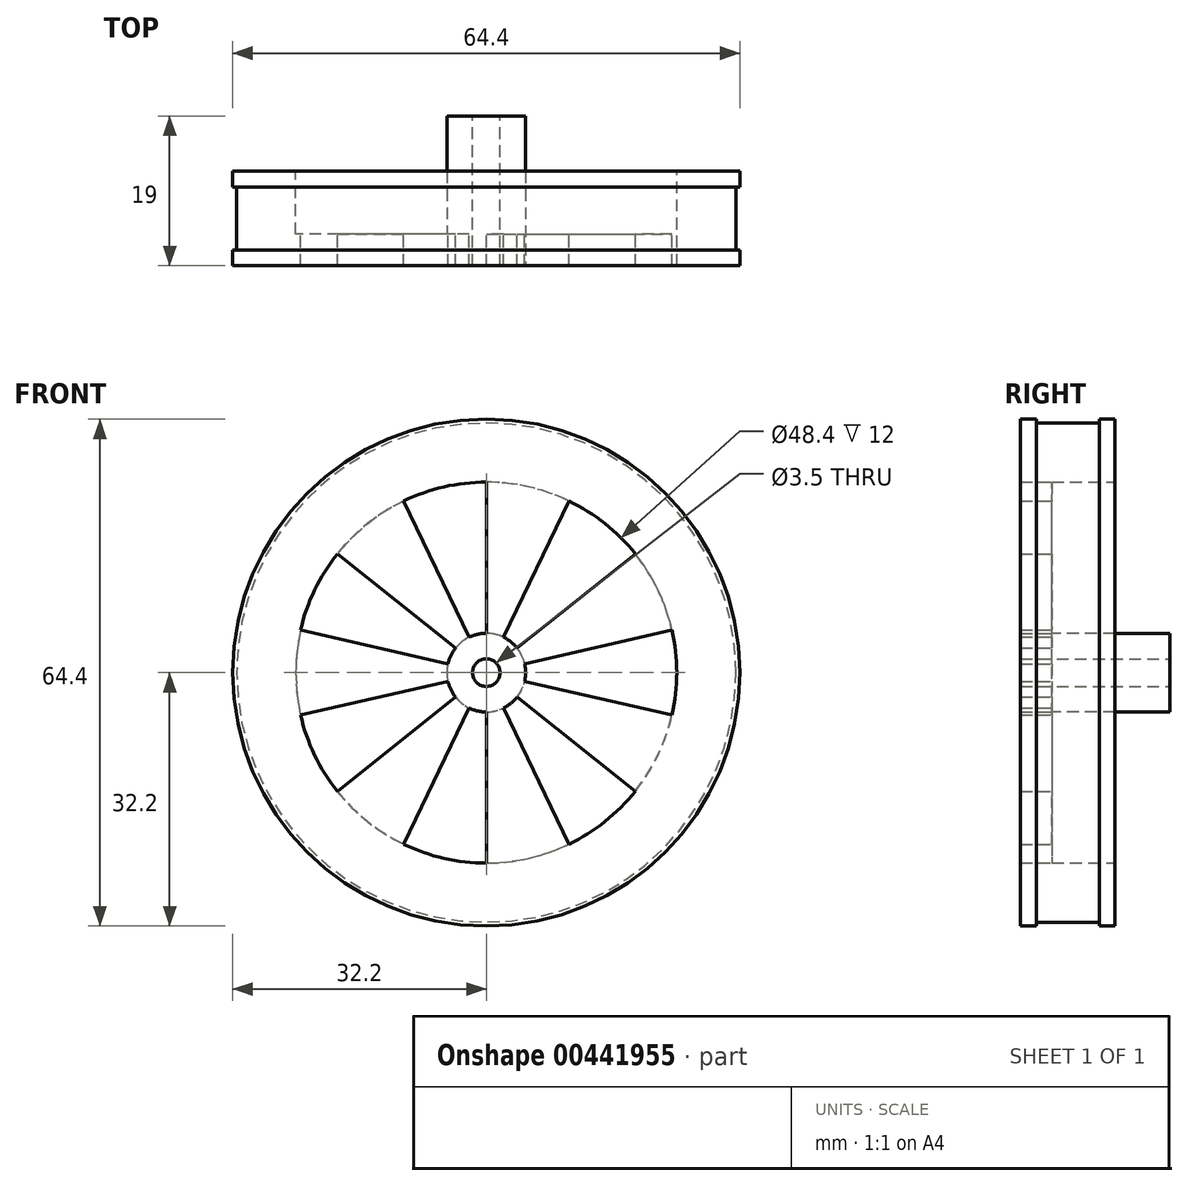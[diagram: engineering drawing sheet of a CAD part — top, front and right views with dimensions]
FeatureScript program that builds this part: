
annotation { "Feature Type Name" : "Feature", "Feature Type Description" : "" }
export const myFeature = defineFeature(function(context is Context, id is Id, definition is map)
    precondition{}
    {
        {
            var Q0;
            Q0=qCreatedBy(makeId("Top.planeOp"),FACE);
            var sketch = newSketch(context, id + "F0", { "sketchPlane" : qUnion([Q0])});
            skLineSegment(sketch, "E0", {"start": v(0, 0) * mm, "end": v(32.2, 0) * mm});
            skLineSegment(sketch, "E1", {"start": v(32.2, 0) * mm, "end": v(32.2, 2) * mm});
            skLineSegment(sketch, "E2", {"start": v(32.2, 2) * mm, "end": v(31.7, 2) * mm});
            skLineSegment(sketch, "E3", {"start": v(31.7, 2) * mm, "end": v(31.7, 10) * mm});
            skLineSegment(sketch, "E4", {"start": v(31.7, 10) * mm, "end": v(32.2, 10) * mm});
            skLineSegment(sketch, "E5", {"start": v(32.2, 10) * mm, "end": v(32.2, 12) * mm});
            skLineSegment(sketch, "E6", {"start": v(32.2, 12) * mm, "end": v(24.2, 12) * mm});
            skLineSegment(sketch, "E7", {"start": v(24.2, 12) * mm, "end": v(24.2, 4) * mm});
            skLineSegment(sketch, "E8", {"start": v(24.2, 4) * mm, "end": v(0, 4) * mm});
            skLineSegment(sketch, "E9", {"start": v(0, 4) * mm, "end": v(0, 0) * mm});
            skSolve(sketch);
        }
        {
            var Q0;
            Q0 = qSketchRegion(id + "F0", true);
            var Q1;
            Q1=sQuery(id+"F0.wireOp",EDGE,"E9");
            revolve(context, id + "F1", {"entities" : qUnion([Q0]), "axis" : qUnion([Q1]), "revolveType" : RevolveType.FULL});
        }
        {
            var Q0;
            Q0=makeQuery(id+"F1.opRevolve","SWEPT_FACE",FACE,{"disambiguationData":[OSD([sQuery(id+"F0.wireOp",EDGE,"E8")])]});
            var sketch = newSketch(context, id + "F2", { "sketchPlane" : qUnion([Q0])});
            skCircle(sketch, "E10", {"center": v(0, 0) * mm, "radius": 5 * mm});
            skSolve(sketch);
        }
        {
            var Q0;
            Q0=makeQuery(id+"F2.imprint","IMPRINT",FACE,{"disambiguationData":[TD([[makeQuery(id+"F2.imprint","IMPRINT",EDGE,{"derivedFrom":sQuery(id+"F2.wireOp",EDGE,"E10")}),1.0]])]});
            extrude(context, id + "F3", {"entities" : qUnion([Q0]), "operationType" : NewBodyOperationType.ADD, "depth" : 15 * mm});
        }
        {
            var Q0;
            Q0=makeQuery(id+"F3.opExtrude","CAP_FACE",FACE,{"disambiguationData":[OSD([sQuery(id+"F2.wireOp",EDGE,"E10")])],"isStart":false});
            var sketch = newSketch(context, id + "F4", { "sketchPlane" : qUnion([Q0])});
            skCircle(sketch, "E11", {"center": v(0, 0) * mm, "radius": 1.75 * mm});
            skSolve(sketch);
        }
        {
            var Q0;
            Q0 = qSketchRegion(id + "F4", true);
            extrude(context, id + "F5", {"entities" : qUnion([Q0]), "operationType" : NewBodyOperationType.REMOVE, "oppositeDirection" : true, "depth" : 25 * mm});
        }
        {
            var Q0;
            Q0=makeQuery(id+"F1.opRevolve","SWEPT_FACE",FACE,{"disambiguationData":[OSD([sQuery(id+"F0.wireOp",EDGE,"E8")])]});
            var sketch = newSketch(context, id + "F6", { "sketchPlane" : qUnion([Q0])});
            skCircle(sketch, "E12.0.0", {"center": v(0, 0) * mm, "radius": 24.2 * mm});
            skLineSegment(sketch, "E13", {"start": v(0, 0) * mm, "end": v(0, 24.2) * mm});
            skLineSegment(sketch, "E14.1.0", {"start": v(0, 0) * mm, "end": v(10.5, 21.8) * mm});
            skLineSegment(sketch, "E14.2.0", {"start": v(0, 0) * mm, "end": v(18.92, 15.09) * mm});
            skLineSegment(sketch, "E14.3.0", {"start": v(0, 0) * mm, "end": v(23.6, 5.39) * mm});
            skLineSegment(sketch, "E14.4.0", {"start": v(0, 0) * mm, "end": v(23.6, -5.39) * mm});
            skLineSegment(sketch, "E14.5.0", {"start": v(0, 0) * mm, "end": v(18.92, -15.09) * mm});
            skLineSegment(sketch, "E14.6.0", {"start": v(0, 0) * mm, "end": v(10.5, -21.8) * mm});
            skLineSegment(sketch, "E14.7.0", {"start": v(0, 0) * mm, "end": v(0, -24.2) * mm});
            skLineSegment(sketch, "E14.anchor1", {"start": v(0, 0) * mm, "end": v(0, 24.2) * mm, "construction": true});
            skLineSegment(sketch, "E14.anchor2", {"start": v(0, 0) * mm, "end": v(0, -24.2) * mm, "construction": true});
            skSolve(sketch);
        }
        {
            var Q0;
            {var subQ0=sQuery(id+"F6.wireOp",EDGE,"E12.0.0");var subQ1=sQuery(id+"F6.wireOp",EDGE,"E14.2.0");var subQ2=makeQuery(id+"F6.imprint","INTERSECT",VERTEX,{"derivedFrom":[subQ1,subQ0]});Q0=makeQuery(id+"F6.imprint","IMPRINT",FACE,{"disambiguationData":[TD([[makeQuery(id+"F6.imprint","IMPRINT",EDGE,{"disambiguationData":[TD([[subQ2,1.0]])],"derivedFrom":subQ1}),-1.0]])]});}
            var Q1;
            {var subQ0=sQuery(id+"F6.wireOp",EDGE,"E12.0.0");var subQ1=sQuery(id+"F6.wireOp",EDGE,"E13");var subQ2=makeQuery(id+"F6.imprint","INTERSECT",VERTEX,{"derivedFrom":[subQ1,subQ0]});Q1=makeQuery(id+"F6.imprint","IMPRINT",FACE,{"disambiguationData":[TD([[makeQuery(id+"F6.imprint","IMPRINT",EDGE,{"disambiguationData":[TD([[subQ2,1.0]])],"derivedFrom":subQ1}),-1.0]])]});}
            var Q2;
            {var subQ0=sQuery(id+"F6.wireOp",EDGE,"E12.0.0");var subQ1=sQuery(id+"F6.wireOp",EDGE,"E14.4.0");var subQ2=makeQuery(id+"F6.imprint","INTERSECT",VERTEX,{"derivedFrom":[subQ1,subQ0]});Q2=makeQuery(id+"F6.imprint","IMPRINT",FACE,{"disambiguationData":[TD([[makeQuery(id+"F6.imprint","IMPRINT",EDGE,{"disambiguationData":[TD([[subQ2,1.0]])],"derivedFrom":subQ1}),-1.0]])]});}
            var Q3;
            {var subQ0=sQuery(id+"F6.wireOp",EDGE,"E12.0.0");var subQ1=sQuery(id+"F6.wireOp",EDGE,"E14.6.0");var subQ2=makeQuery(id+"F6.imprint","INTERSECT",VERTEX,{"derivedFrom":[subQ1,subQ0]});Q3=makeQuery(id+"F6.imprint","IMPRINT",FACE,{"disambiguationData":[TD([[makeQuery(id+"F6.imprint","IMPRINT",EDGE,{"disambiguationData":[TD([[subQ2,1.0]])],"derivedFrom":subQ1}),-1.0]])]});}
            extrude(context, id + "F7", {"entities" : qUnion([Q0, Q1, Q2, Q3]), "operationType" : NewBodyOperationType.REMOVE, "oppositeDirection" : true, "depth" : 25 * mm});
        }
        {
            var Q0;
            {var subQ4=sQuery(id+"F6.wireOp",EDGE,"E13");Q0=makeQuery(id+"F7.boolean.opBoolean","SPLIT",FACE,{"disambiguationData":[TD([makeQuery(id+"F7.opExtrude","SWEPT_FACE",FACE,{"disambiguationData":[OSD([subQ4])]})])],"derivedFrom":makeQuery(id+"F1.opRevolve","SWEPT_FACE",FACE,{"disambiguationData":[OSD([sQuery(id+"F0.wireOp",EDGE,"E8")])]})});}
            var sketch = newSketch(context, id + "F8", { "sketchPlane" : qUnion([Q0])});
            skLineSegment(sketch, "E15", {"start": v(0, 0) * mm, "end": v(0, -24.2) * mm});
            skLineSegment(sketch, "E16.1.0", {"start": v(0, 0) * mm, "end": v(-10.5, -21.8) * mm});
            skLineSegment(sketch, "E16.2.0", {"start": v(0, 0) * mm, "end": v(-18.92, -15.09) * mm});
            skLineSegment(sketch, "E16.3.0", {"start": v(0, 0) * mm, "end": v(-23.6, -5.39) * mm});
            skLineSegment(sketch, "E16.4.0", {"start": v(0, 0) * mm, "end": v(-23.6, 5.39) * mm});
            skLineSegment(sketch, "E16.5.0", {"start": v(0, 0) * mm, "end": v(-18.92, 15.09) * mm});
            skLineSegment(sketch, "E16.6.0", {"start": v(0, 0) * mm, "end": v(-10.5, 21.8) * mm});
            skLineSegment(sketch, "E16.7.0", {"start": v(0, 0) * mm, "end": v(0, 24.2) * mm});
            skPoint(sketch, "E16.center", {"position": v(0, 0) * mm});
            skLineSegment(sketch, "E16.anchor1", {"start": v(0, 0) * mm, "end": v(0, -24.2) * mm, "construction": true});
            skLineSegment(sketch, "E16.anchor2", {"start": v(0, 0) * mm, "end": v(0, 24.2) * mm, "construction": true});
            skSolve(sketch);
        }
        {
            var Q0;
            {var subQ0=sQuery(id+"F8.wireOp",EDGE,"E16.3.0");var subQ3=sQuery(id+"F6.wireOp",EDGE,"E13");var subQ4=makeQuery(id+"F7.opExtrude","SWEPT_FACE",FACE,{"disambiguationData":[OSD([subQ3])]});var subQ17=sQuery(id+"F2.wireOp",EDGE,"E10");var subQ18=makeQuery(id+"F3.opExtrude","CAP_EDGE",EDGE,{"disambiguationData":[OSD([subQ17])],"isStart":true});var subQ19=makeQuery(id+"F7.boolean.opBoolean","SPLIT",EDGE,{"disambiguationData":[TD([subQ4])],"derivedFrom":subQ18});var subQ20=makeQuery(id+"F8.imprint","INTERSECT",VERTEX,{"derivedFrom":[subQ19,subQ0]});Q0=makeQuery(id+"F8.imprint","IMPRINT",FACE,{"disambiguationData":[TD([[makeQuery(id+"F8.imprint","IMPRINT",EDGE,{"disambiguationData":[TD([[subQ20,-1.0]])],"derivedFrom":subQ0}),-1.0]])]});}
            var Q1;
            {var subQ0=sQuery(id+"F8.wireOp",EDGE,"E16.5.0");var subQ3=sQuery(id+"F6.wireOp",EDGE,"E13");var subQ4=makeQuery(id+"F7.opExtrude","SWEPT_FACE",FACE,{"disambiguationData":[OSD([subQ3])]});var subQ17=sQuery(id+"F2.wireOp",EDGE,"E10");var subQ18=makeQuery(id+"F3.opExtrude","CAP_EDGE",EDGE,{"disambiguationData":[OSD([subQ17])],"isStart":true});var subQ19=makeQuery(id+"F7.boolean.opBoolean","SPLIT",EDGE,{"disambiguationData":[TD([subQ4])],"derivedFrom":subQ18});var subQ20=makeQuery(id+"F8.imprint","INTERSECT",VERTEX,{"derivedFrom":[subQ19,subQ0]});Q1=makeQuery(id+"F8.imprint","IMPRINT",FACE,{"disambiguationData":[TD([[makeQuery(id+"F8.imprint","IMPRINT",EDGE,{"disambiguationData":[TD([[subQ20,-1.0]])],"derivedFrom":subQ0}),-1.0]])]});}
            var Q2;
            {var subQ0=sQuery(id+"F8.wireOp",EDGE,"E16.1.0");var subQ3=sQuery(id+"F6.wireOp",EDGE,"E13");var subQ4=makeQuery(id+"F7.opExtrude","SWEPT_FACE",FACE,{"disambiguationData":[OSD([subQ3])]});var subQ17=sQuery(id+"F2.wireOp",EDGE,"E10");var subQ18=makeQuery(id+"F3.opExtrude","CAP_EDGE",EDGE,{"disambiguationData":[OSD([subQ17])],"isStart":true});var subQ19=makeQuery(id+"F7.boolean.opBoolean","SPLIT",EDGE,{"disambiguationData":[TD([subQ4])],"derivedFrom":subQ18});var subQ20=makeQuery(id+"F8.imprint","INTERSECT",VERTEX,{"derivedFrom":[subQ19,subQ0]});Q2=makeQuery(id+"F8.imprint","IMPRINT",FACE,{"disambiguationData":[TD([[makeQuery(id+"F8.imprint","IMPRINT",EDGE,{"disambiguationData":[TD([[subQ20,-1.0]])],"derivedFrom":subQ0}),-1.0]])]});}
            extrude(context, id + "F9", {"entities" : qUnion([Q0, Q1, Q2]), "operationType" : NewBodyOperationType.REMOVE, "oppositeDirection" : true, "depth" : 25 * mm});
        }
    });
